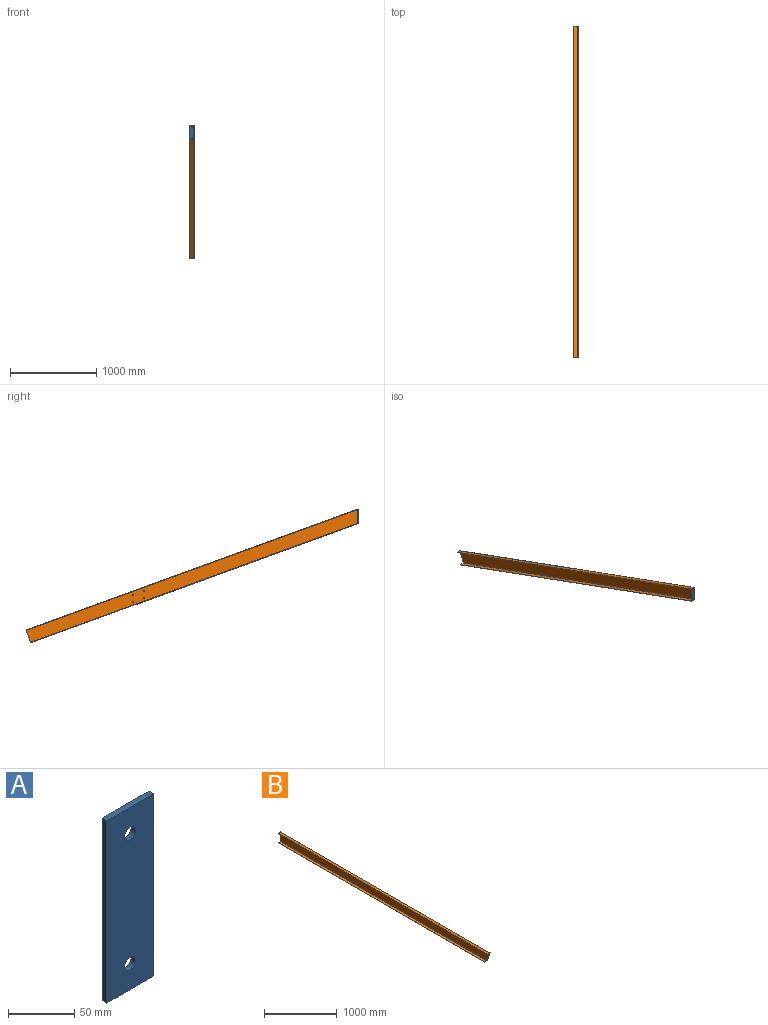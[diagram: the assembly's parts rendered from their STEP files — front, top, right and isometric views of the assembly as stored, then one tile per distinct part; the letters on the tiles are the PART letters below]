
ASSEMBLY  parts=2 mates=1
PART A: 8 faces, bbox 50x5x168 mm
  f0: plane 50x5mm, normal (0,0,1), area 250mm2, adj f1,f3,f4,f5
  f1: plane 168x5mm, normal (-1,0,0), area 840mm2, adj f0,f2,f4,f5
  f2: plane 50x5mm, normal (0,0,-1), area 250mm2, adj f1,f3,f4,f5
  f3: plane 168x5mm, normal (1,0,0), area 840mm2, adj f0,f2,f4,f5
  f4: plane 168x50mm, normal (0,-1,0), area 8173.8mm2, adj f0,f1,f2,f3,f6,f7
  f5: plane 168x50mm, normal (0,1,0), area 8173.8mm2, adj f0,f1,f2,f3,f6,f7
  f6: cylinder r=6mm len=12mm, axis (0,-1,0), area 188.5mm2, adj f4,f5
  f7: cylinder r=6mm len=12mm, axis (0,-1,0), area 188.5mm2, adj f4,f5
PART B: 26 faces, bbox 50x4081x160 mm
  f0: plane 44x2mm, normal (0,1,0), area 88mm2, adj f2,f3,f4,f23
  f1: plane 44x2mm, normal (0,-1,0), area 88mm2, adj f2,f3,f4,f22
  f2: plane 4081x2mm, normal (-1,0,0), area 8162mm2, adj f0,f1,f3,f4
  f3: plane 4081x44mm, normal (0,0,-1), area 179564mm2, adj f0,f1,f2,f25
  f4: plane 4081x44mm, normal (0,0,1), area 179564mm2, adj f0,f1,f2,f24
  f5: plane 148x2mm, normal (0,1,0), area 296mm2, adj f11,f12,f19,f23
  f6: plane 148x53.87mm, normal (0,-0.94,-0.34), area 315mm2, adj f11,f12,f18,f22
  f7: cylinder r=6mm len=12mm, axis (-1,0,0), area 75.4mm2, adj f11,f12
  f8: cylinder r=6mm len=12mm, axis (-1,0,0), area 75.4mm2, adj f11,f12
  f9: cylinder r=6mm len=12mm, axis (-1,0,0), area 75.4mm2, adj f11,f12
  f10: cylinder r=6mm len=12mm, axis (-1,0,0), area 75.4mm2, adj f11,f12
  f11: plane 4078.82x148mm, normal (-1,0,0), area 599226.2mm2, adj f5,f6,f7,f8,f9,f10,f21,f25
  f12: plane 4078.82x148mm, normal (1,0,0), area 599226.2mm2, adj f5,f6,f7,f8,f9,f10,f20,f24
  f13: plane 44x2mm, normal (0,1,0), area 88mm2, adj f14,f16,f17,f19
  f14: plane 4022.76x2mm, normal (-1,0,0), area 8045.5mm2, adj f13,f15,f16,f17
  f15: plane 44x2mm, normal (0,-1,0), area 88mm2, adj f14,f16,f17,f18
  f16: plane 4022.76x44mm, normal (0,0,1), area 177001.6mm2, adj f13,f14,f15,f21
  f17: plane 4022.76x44mm, normal (0,0,-1), area 177001.6mm2, adj f13,f14,f15,f20
  f18: bspline ~6x6mm, area 16.4mm2, adj f6,f15,f20,f21
  f19: plane 6x6mm, normal (0,1,0), area 15.7mm2, adj f5,f13,f20,f21
  f20: cylinder r=6mm len=4024.95mm, axis (0,-1,0), area 37921.2mm2, adj f12,f17,f18,f19
  f21: cylinder r=4mm len=4024.95mm, axis (0,-1,0), area 25280.8mm2, adj f11,f16,f18,f19
  f22: bspline ~6x6mm, area 16.5mm2, adj f1,f6,f24,f25
  f23: plane 6x6mm, normal (0,1,0), area 15.7mm2, adj f0,f5,f24,f25
  f24: cylinder r=6mm len=4081mm, axis (0,-1,0), area 38452.2mm2, adj f4,f12,f22,f23
  f25: cylinder r=4mm len=4081mm, axis (0,-1,0), area 25634.8mm2, adj f3,f11,f22,f23
PLACE A t=(-977.94,-949.92,-453.06)mm
PLACE B rot(axis=(-1,0,0),20deg) t=(-977.94,942.67,-1140.99)mm
MATE fastened A.f3 <-> B.f12  axis (1,0,0) through (-952.94,-947.42,-453.06)mm
